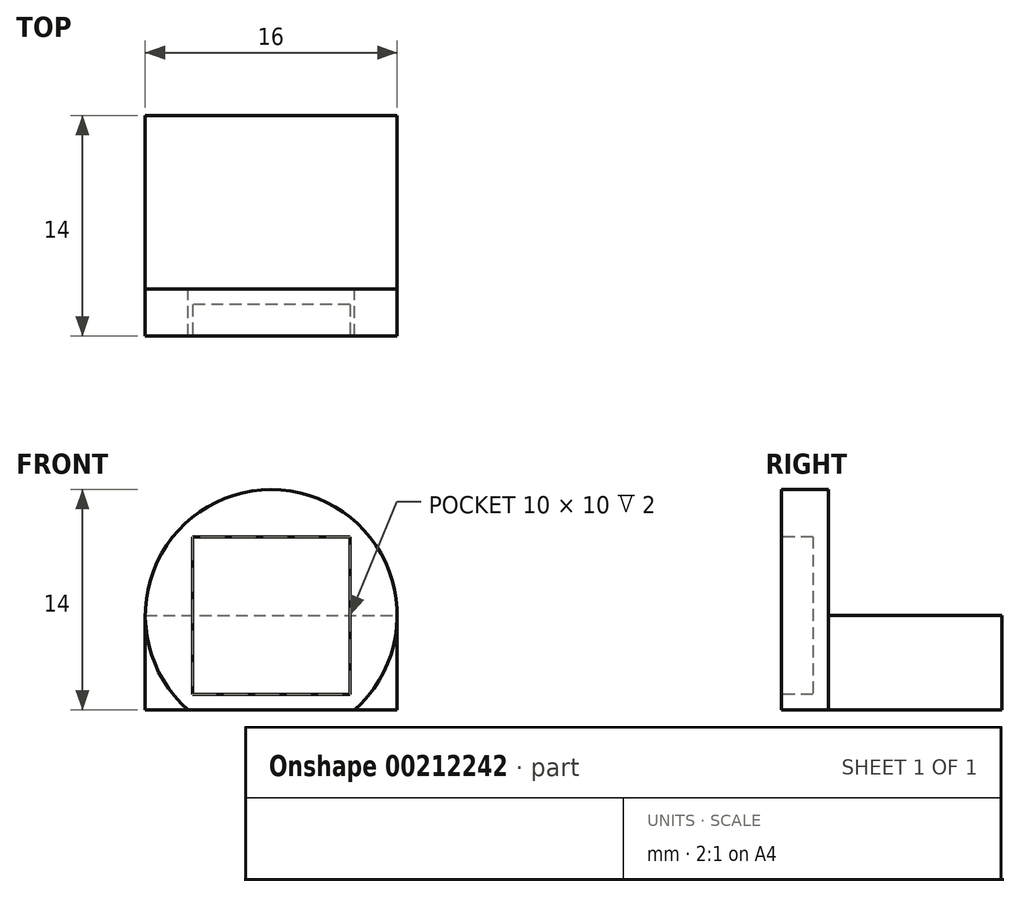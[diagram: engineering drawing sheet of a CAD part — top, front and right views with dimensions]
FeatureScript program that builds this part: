
annotation { "Feature Type Name" : "Feature", "Feature Type Description" : "" }
export const myFeature = defineFeature(function(context is Context, id is Id, definition is map)
    precondition{}
    {
        {
            var Q0;
            Q0=qCreatedBy(makeId("Front.planeOp"),FACE);
            var sketch = newSketch(context, id + "F0", { "sketchPlane" : qUnion([Q0])});
            skCircle(sketch, "E0", {"center": v(0, 0) * mm, "radius": 8 * mm});
            skLineSegment(sketch, "E1", {"start": v(-8, 0) * mm, "end": v(-8, -6) * mm});
            skLineSegment(sketch, "E2", {"start": v(-8, -6) * mm, "end": v(8, -6) * mm});
            skLineSegment(sketch, "E3", {"start": v(8, -6) * mm, "end": v(8, 0) * mm});
            skLineSegment(sketch, "E4", {"start": v(-8, 0) * mm, "end": v(8, 0) * mm});
            skSolve(sketch);
        }
        {
            var Q0;
            {var subQ0=sQuery(id+"F0.wireOp",EDGE,"E1");Q0=makeQuery(id+"F0.imprint","IMPRINT",FACE,{"disambiguationData":[TD([[makeQuery(id+"F0.imprint","IMPRINT",EDGE,{"derivedFrom":subQ0}),1.0]])]});}
            var Q1;
            {var subQ0=sQuery(id+"F0.wireOp",EDGE,"E3");Q1=makeQuery(id+"F0.imprint","IMPRINT",FACE,{"disambiguationData":[TD([[makeQuery(id+"F0.imprint","IMPRINT",EDGE,{"derivedFrom":subQ0}),1.0]])]});}
            var Q2;
            {var subQ0=sQuery(id+"F0.wireOp",EDGE,"E4");Q2=makeQuery(id+"F0.imprint","IMPRINT",FACE,{"disambiguationData":[TD([[makeQuery(id+"F0.imprint","IMPRINT",EDGE,{"derivedFrom":subQ0}),-1.0]])]});}
            extrude(context, id + "F1", {"entities" : qUnion([Q0, Q1, Q2]), "oppositeDirection" : true, "depth" : 11 * mm});
        }
        {
            var Q0;
            {var subQ0=sQuery(id+"F0.wireOp",EDGE,"E4");Q0=makeQuery(id+"F0.imprint","IMPRINT",FACE,{"disambiguationData":[TD([[makeQuery(id+"F0.imprint","IMPRINT",EDGE,{"derivedFrom":subQ0}),1.0]])]});}
            var Q1;
            {var subQ0=sQuery(id+"F0.wireOp",EDGE,"E4");Q1=makeQuery(id+"F0.imprint","IMPRINT",FACE,{"disambiguationData":[TD([[makeQuery(id+"F0.imprint","IMPRINT",EDGE,{"derivedFrom":subQ0}),-1.0]])]});}
            var Q2;
            {var subQ0=sQuery(id+"F0.wireOp",EDGE,"E2");var subQ1=sQuery(id+"F0.wireOp",EDGE,"E0");var subQ2=makeQuery(id+"F0.imprint","INTERSECT",VERTEX,{"disambiguationData":[OD(0.0)],"derivedFrom":[subQ1,subQ0]});Q2=makeQuery(id+"F0.imprint","IMPRINT",FACE,{"disambiguationData":[TD([[makeQuery(id+"F0.imprint","IMPRINT",EDGE,{"disambiguationData":[TD([[subQ2,-1.0]])],"derivedFrom":subQ1}),1.0]])]});}
            extrude(context, id + "F2", {"entities" : qUnion([Q0, Q1, Q2]), "operationType" : NewBodyOperationType.ADD, "depth" : 3 * mm});
        }
        {
            var Q0;
            Q0=makeQuery(id+"F2.opExtrude","CAP_FACE",FACE,{"disambiguationData":[OSD([sQuery(id+"F0.wireOp",EDGE,"E0")])],"isStart":false});
            var sketch = newSketch(context, id + "F3", { "sketchPlane" : qUnion([Q0])});
            skLineSegment(sketch, "E5.bottom", {"start": v(5, 5) * mm, "end": v(-5, 5) * mm});
            skLineSegment(sketch, "E5.top", {"start": v(5, -5) * mm, "end": v(-5, -5) * mm});
            skLineSegment(sketch, "E5.left", {"start": v(5, 5) * mm, "end": v(5, -5) * mm});
            skLineSegment(sketch, "E5.right", {"start": v(-5, 5) * mm, "end": v(-5, -5) * mm});
            skPoint(sketch, "E5.middle", {"position": v(0, 0) * mm});
            skSolve(sketch);
        }
        {
            var Q0;
            Q0=makeQuery(id+"F3.imprint","IMPRINT",FACE,{"disambiguationData":[TD([[makeQuery(id+"F3.imprint","IMPRINT",EDGE,{"derivedFrom":sQuery(id+"F3.wireOp",EDGE,"E5.bottom")}),1.0]])]});
            extrude(context, id + "F4", {"entities" : qUnion([Q0]), "operationType" : NewBodyOperationType.REMOVE, "oppositeDirection" : true, "depth" : 2 * mm});
        }
    });
